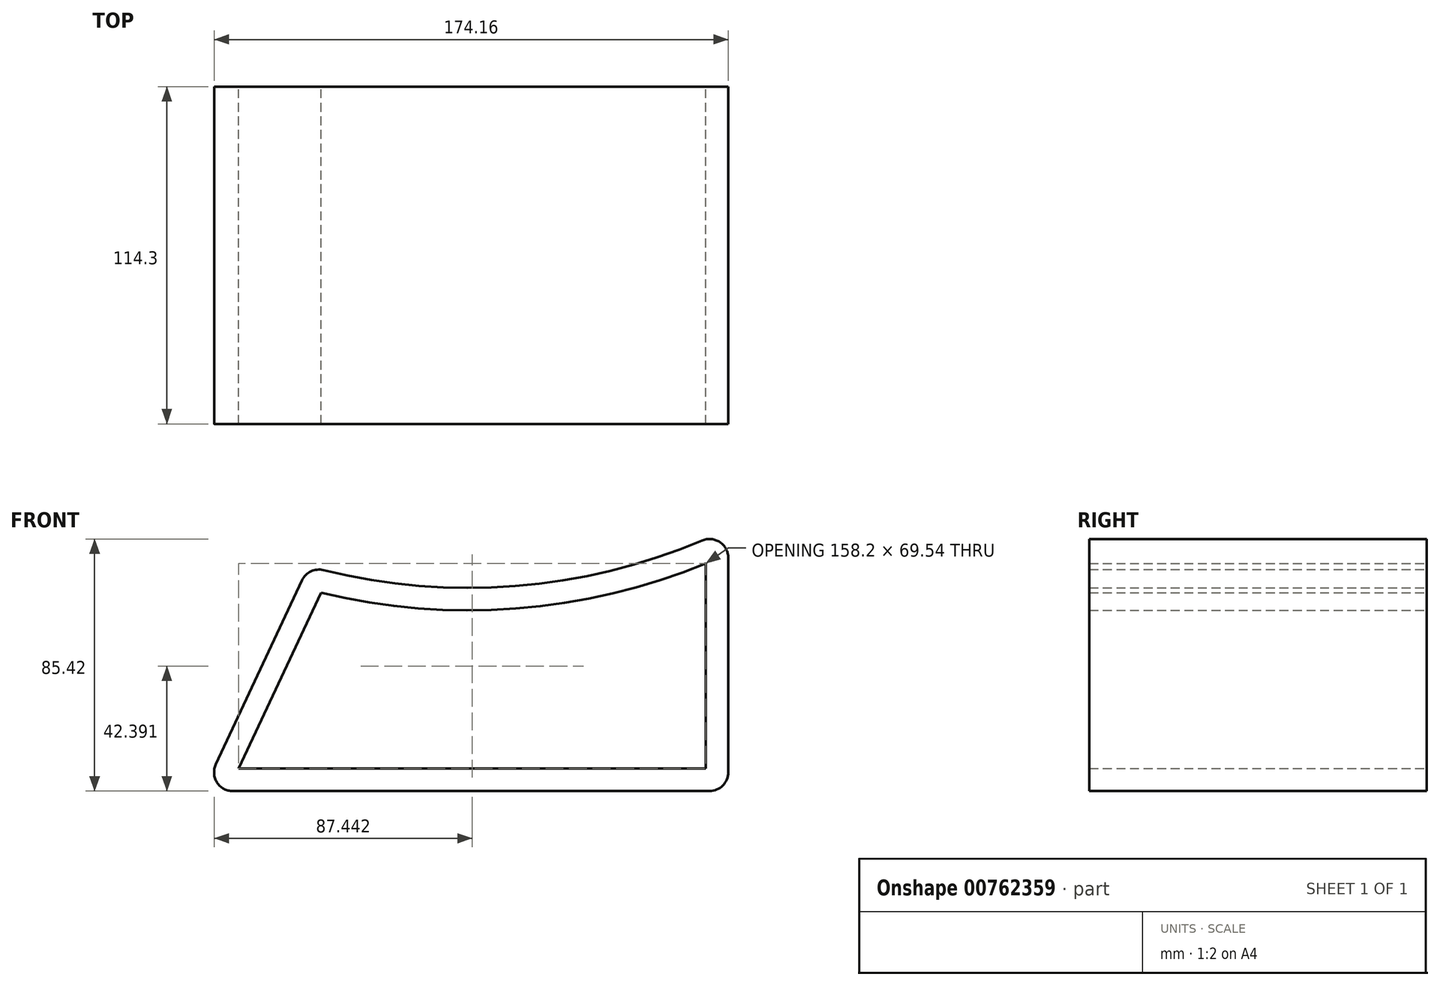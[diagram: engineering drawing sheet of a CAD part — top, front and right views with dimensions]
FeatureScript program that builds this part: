
annotation { "Feature Type Name" : "Feature", "Feature Type Description" : "" }
export const myFeature = defineFeature(function(context is Context, id is Id, definition is map)
    precondition{}
    {
        {
            var Q0;
            Q0=qCreatedBy(makeId("Front.planeOp"),FACE);
            var sketch = newSketch(context, id + "F0", { "sketchPlane" : qUnion([Q0])});
            skLineSegment(sketch, "E0.top", {"start": v(82.55, -44.45) * mm, "end": v(-78.91, -44.45) * mm});
            skLineSegment(sketch, "E0.left", {"start": v(88.9, 34.62) * mm, "end": v(88.9, -38.1) * mm});
            skPoint(sketch, "E0.middle", {"position": v(0, 0) * mm});
            skLineSegment(sketch, "E1", {"start": v(-55.45, 26.96) * mm, "end": v(-84.66, -35.4) * mm});
            skArc(sketch, "E2", {"start": v(-48.16, 30.43) * mm, "mid": v(16.77, 25.03) * mm, "end": v(80.08, 40.47) * mm});
            skPoint(sketch, "E0.right.start.orphan", {"position": v(-88.9, 44.45) * mm});
            skPoint(sketch, "E3.visualSharp", {"position": v(88.9, 44.45) * mm});
            skArc(sketch, "E3.filletArc", {"start": v(88.9, 34.62) * mm, "mid": v(86.06, 39.91) * mm, "end": v(80.08, 40.47) * mm});
            skPoint(sketch, "E4.visualSharp", {"position": v(88.9, -44.45) * mm});
            skArc(sketch, "E4.filletArc", {"start": v(82.55, -44.45) * mm, "mid": v(87.04, -42.6) * mm, "end": v(88.9, -38.1) * mm});
            skPoint(sketch, "E5.visualSharp", {"position": v(-88.9, -44.45) * mm});
            skArc(sketch, "E5.filletArc", {"start": v(-84.66, -35.4) * mm, "mid": v(-84.27, -41.5) * mm, "end": v(-78.91, -44.45) * mm});
            skPoint(sketch, "E6.visualSharp", {"position": v(-53.2, 31.75) * mm});
            skArc(sketch, "E6.filletArc", {"start": v(-48.16, 30.43) * mm, "mid": v(-52.43, 30) * mm, "end": v(-55.45, 26.96) * mm});
            skLineSegment(sketch, "E7.0", {"start": v(81.28, 32.71) * mm, "end": v(81.28, -36.83) * mm});
            skArc(sketch, "E7.1", {"start": v(-48.99, 22.78) * mm, "mid": v(16.93, 17.4) * mm, "end": v(81.28, 32.71) * mm});
            skLineSegment(sketch, "E7.2", {"start": v(-48.99, 22.78) * mm, "end": v(-76.92, -36.83) * mm});
            skLineSegment(sketch, "E7.3", {"start": v(81.28, -36.83) * mm, "end": v(-76.92, -36.83) * mm});
            skSolve(sketch);
        }
        {
            var Q0;
            Q0 = qSketchRegion(id + "F0", true);
            extrude(context, id + "F1", {"entities" : qUnion([Q0]), "depth" : 114.3 * mm, "offsetDistance" : 25.4 * mm});
        }
    });
